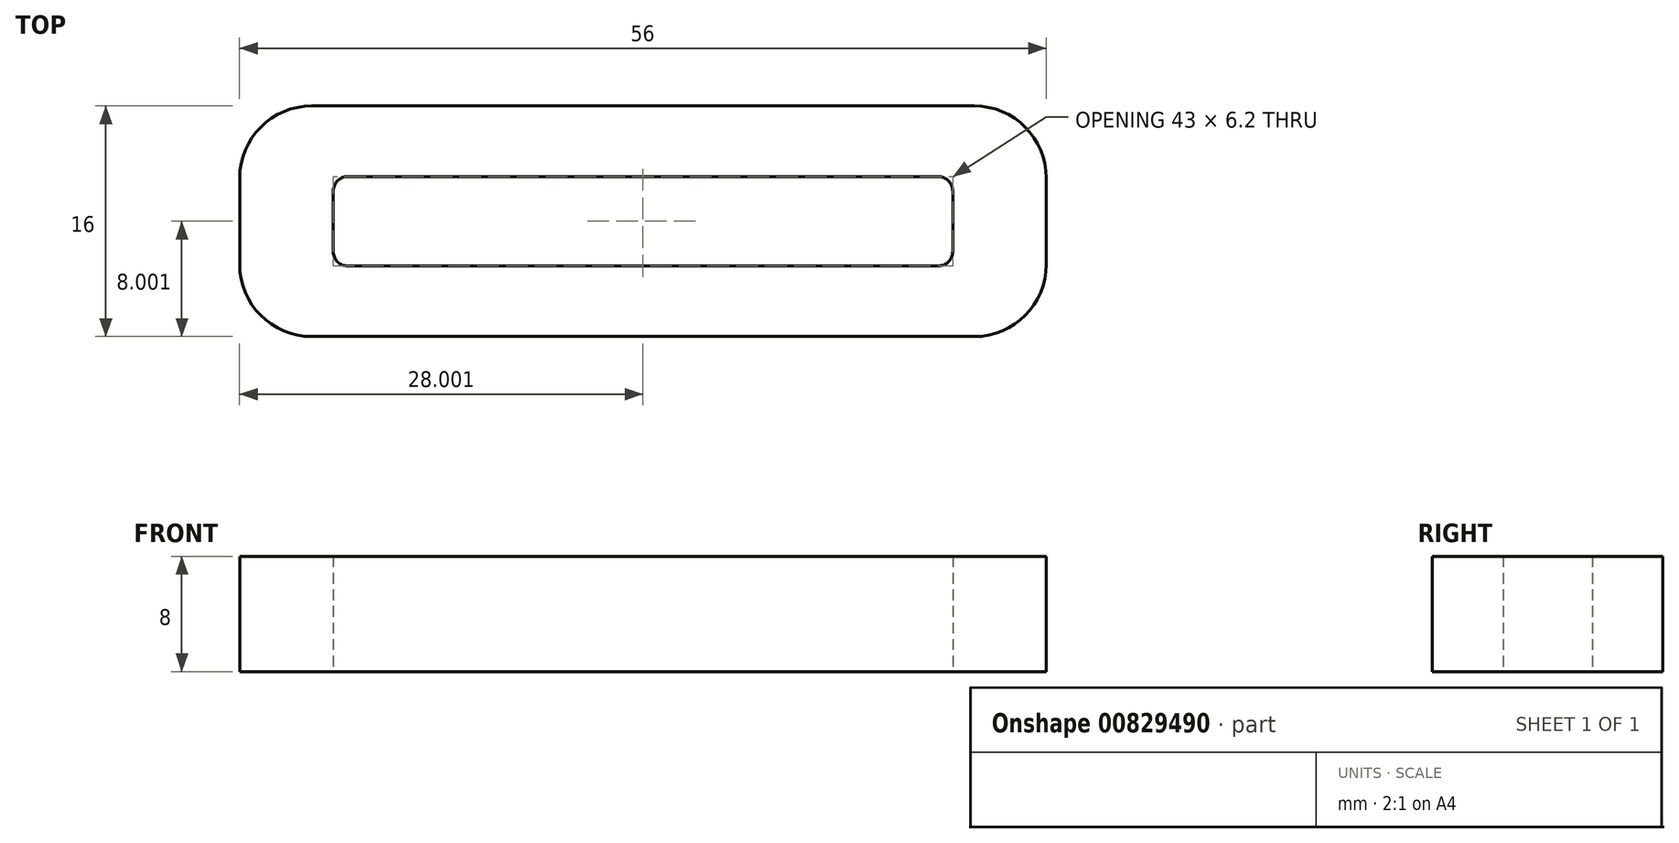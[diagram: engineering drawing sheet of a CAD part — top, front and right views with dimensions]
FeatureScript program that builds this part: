
annotation { "Feature Type Name" : "Feature", "Feature Type Description" : "" }
export const myFeature = defineFeature(function(context is Context, id is Id, definition is map)
    precondition{}
    {
        {
            var Q0;
            Q0=qCreatedBy(makeId("Top.planeOp"),FACE);
            var sketch = newSketch(context, id + "F0", { "sketchPlane" : qUnion([Q0])});
            skLineSegment(sketch, "E0.bottom", {"start": v(-15.09, 8.91) * mm, "end": v(30.91, 8.91) * mm});
            skLineSegment(sketch, "E0.top", {"start": v(-15.09, -7.09) * mm, "end": v(30.91, -7.09) * mm});
            skLineSegment(sketch, "E0.left", {"start": v(-20.09, 3.91) * mm, "end": v(-20.09, 0.91) * mm});
            skLineSegment(sketch, "E0.right", {"start": v(35.91, 3.91) * mm, "end": v(35.91, 0.91) * mm});
            skLineSegment(sketch, "E1", {"start": v(-20.09, 0.91) * mm, "end": v(-20.09, -2.09) * mm});
            skLineSegment(sketch, "E2", {"start": v(35.91, 0.91) * mm, "end": v(35.91, -2.09) * mm});
            skLineSegment(sketch, "E3", {"start": v(-20.09, 0.91) * mm, "end": v(-13.59, 0.91) * mm, "construction": true});
            skLineSegment(sketch, "E4", {"start": v(-13.59, 0.91) * mm, "end": v(29.41, 0.91) * mm, "construction": true});
            skLineSegment(sketch, "E5", {"start": v(29.41, 0.91) * mm, "end": v(35.91, 0.91) * mm, "construction": true});
            skLineSegment(sketch, "E6", {"start": v(-13.59, 0.91) * mm, "end": v(-13.59, 3.01) * mm});
            skLineSegment(sketch, "E7", {"start": v(-13.59, 0.91) * mm, "end": v(-13.59, -1.19) * mm});
            skLineSegment(sketch, "E8", {"start": v(29.41, 0.91) * mm, "end": v(29.41, 3.01) * mm});
            skLineSegment(sketch, "E9", {"start": v(29.41, 0.91) * mm, "end": v(29.41, -1.19) * mm});
            skLineSegment(sketch, "E10", {"start": v(28.41, 4.01) * mm, "end": v(-12.59, 4.01) * mm});
            skLineSegment(sketch, "E11", {"start": v(-12.59, -2.19) * mm, "end": v(28.41, -2.19) * mm});
            skPoint(sketch, "E12.visualSharp", {"position": v(-20.09, 8.91) * mm});
            skArc(sketch, "E12.filletArc", {"start": v(-15.09, 8.91) * mm, "mid": v(-18.62, 7.45) * mm, "end": v(-20.09, 3.91) * mm});
            skPoint(sketch, "E13.visualSharp", {"position": v(-20.09, -7.09) * mm});
            skArc(sketch, "E13.filletArc", {"start": v(-20.09, -2.09) * mm, "mid": v(-18.62, -5.62) * mm, "end": v(-15.09, -7.09) * mm});
            skPoint(sketch, "E14.visualSharp", {"position": v(35.91, -7.09) * mm});
            skArc(sketch, "E14.filletArc", {"start": v(30.91, -7.09) * mm, "mid": v(34.45, -5.62) * mm, "end": v(35.91, -2.09) * mm});
            skPoint(sketch, "E15.visualSharp", {"position": v(35.91, 8.91) * mm});
            skArc(sketch, "E15.filletArc", {"start": v(35.91, 3.91) * mm, "mid": v(34.45, 7.45) * mm, "end": v(30.91, 8.91) * mm});
            skPoint(sketch, "E16.visualSharp", {"position": v(-13.59, 4.01) * mm});
            skArc(sketch, "E16.filletArc", {"start": v(-12.59, 4.01) * mm, "mid": v(-13.3, 3.72) * mm, "end": v(-13.59, 3.01) * mm});
            skPoint(sketch, "E17.visualSharp", {"position": v(-13.59, -2.19) * mm});
            skArc(sketch, "E17.filletArc", {"start": v(-13.59, -1.19) * mm, "mid": v(-13.3, -1.9) * mm, "end": v(-12.59, -2.19) * mm});
            skPoint(sketch, "E18.visualSharp", {"position": v(29.41, 4.01) * mm});
            skArc(sketch, "E18.filletArc", {"start": v(29.41, 3.01) * mm, "mid": v(29.12, 3.72) * mm, "end": v(28.41, 4.01) * mm});
            skPoint(sketch, "E19.visualSharp", {"position": v(29.41, -2.19) * mm});
            skArc(sketch, "E19.filletArc", {"start": v(28.41, -2.19) * mm, "mid": v(29.12, -1.9) * mm, "end": v(29.41, -1.19) * mm});
            skSolve(sketch);
        }
        {
            var Q0;
            Q0=makeQuery(id+"F0.imprint","IMPRINT",FACE,{"disambiguationData":[TD([[makeQuery(id+"F0.imprint","IMPRINT",EDGE,{"derivedFrom":sQuery(id+"F0.wireOp",EDGE,"E0.bottom")}),-1.0]])]});
            extrude(context, id + "F1", {"entities" : qUnion([Q0]), "depth" : 8 * mm, "offsetDistance" : 25 * mm});
        }
    });
